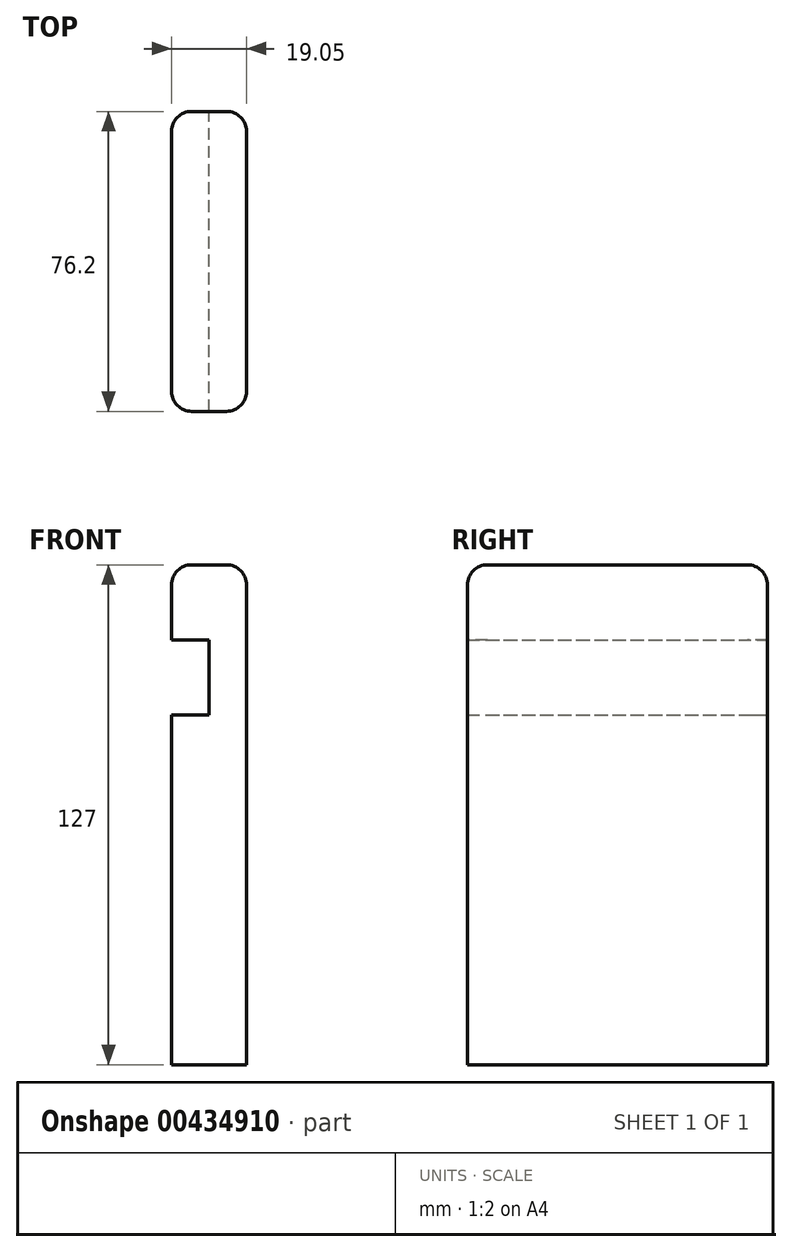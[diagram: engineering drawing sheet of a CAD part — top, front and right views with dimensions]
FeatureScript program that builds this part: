
annotation { "Feature Type Name" : "Feature", "Feature Type Description" : "" }
export const myFeature = defineFeature(function(context is Context, id is Id, definition is map)
    precondition{}
    {
        {
            var Q0;
            Q0=qCreatedBy(makeId("Front.planeOp"),FACE);
            var sketch = newSketch(context, id + "F0", { "sketchPlane" : qUnion([Q0])});
            skLineSegment(sketch, "E0", {"start": v(0, -60.45) * mm, "end": v(19.05, -60.45) * mm});
            skLineSegment(sketch, "E1", {"start": v(19.05, -60.45) * mm, "end": v(19.05, 66.55) * mm});
            skLineSegment(sketch, "E2", {"start": v(19.05, 66.55) * mm, "end": v(0, 66.55) * mm});
            skLineSegment(sketch, "E3", {"start": v(0, 66.55) * mm, "end": v(0, 47.5) * mm});
            skLineSegment(sketch, "E4", {"start": v(0, 47.5) * mm, "end": v(9.53, 47.5) * mm});
            skLineSegment(sketch, "E5", {"start": v(9.53, 47.5) * mm, "end": v(9.53, 28.45) * mm});
            skLineSegment(sketch, "E6", {"start": v(9.53, 28.45) * mm, "end": v(0, 28.45) * mm});
            skLineSegment(sketch, "E7", {"start": v(0, 28.45) * mm, "end": v(0, -60.45) * mm});
            skSolve(sketch);
        }
        {
            var Q0;
            Q0 = qSketchRegion(id + "F0", true);
            extrude(context, id + "F1", {"entities" : qUnion([Q0]), "depth" : 76.2 * mm});
        }
        {
            var Q0;
            Q0=makeQuery(id+"F1.opExtrude","CAP_EDGE",EDGE,{"disambiguationData":[OSD([sQuery(id+"F0.wireOp",EDGE,"E7")])],"isStart":false});
            var Q1;
            Q1=makeQuery(id+"F1.opExtrude","CAP_EDGE",EDGE,{"disambiguationData":[OSD([sQuery(id+"F0.wireOp",EDGE,"E7")])],"isStart":true});
            var Q2;
            Q2=makeQuery(id+"F1.opExtrude","CAP_EDGE",EDGE,{"disambiguationData":[OSD([sQuery(id+"F0.wireOp",EDGE,"E2")])],"isStart":false});
            var Q3;
            Q3=makeQuery(id+"F1.opExtrude","SWEPT_EDGE",EDGE,{"disambiguationData":[OSD([sQuery(id+"F0.wireOp",EDGE,"E2"),sQuery(id+"F0.wireOp",EDGE,"E3")])]});
            var Q4;
            Q4=makeQuery(id+"F1.opExtrude","CAP_EDGE",EDGE,{"disambiguationData":[OSD([sQuery(id+"F0.wireOp",EDGE,"E1")])],"isStart":false});
            var Q5;
            Q5=makeQuery(id+"F1.opExtrude","SWEPT_EDGE",EDGE,{"disambiguationData":[OSD([sQuery(id+"F0.wireOp",EDGE,"E1"),sQuery(id+"F0.wireOp",EDGE,"E2")])]});
            var Q6;
            Q6=makeQuery(id+"F1.opExtrude","CAP_EDGE",EDGE,{"disambiguationData":[OSD([sQuery(id+"F0.wireOp",EDGE,"E2")])],"isStart":true});
            var Q7;
            Q7=makeQuery(id+"F1.opExtrude","CAP_EDGE",EDGE,{"disambiguationData":[OSD([sQuery(id+"F0.wireOp",EDGE,"E1")])],"isStart":true});
            var Q8;
            Q8=makeQuery(id+"F1.opExtrude","CAP_EDGE",EDGE,{"disambiguationData":[OSD([sQuery(id+"F0.wireOp",EDGE,"E3")])],"isStart":true});
            var Q9;
            Q9=makeQuery(id+"F1.opExtrude","CAP_EDGE",EDGE,{"disambiguationData":[OSD([sQuery(id+"F0.wireOp",EDGE,"E3")])],"isStart":false});
            fillet(context, id + "F2", {"entities" : qUnion([Q0, Q1, Q2, Q3, Q4, Q5, Q6, Q7, Q8, Q9]), "radius" : 5.08 * mm, "tangentPropagation" : true, "allowEdgeOverflow" : false});
        }
    });
